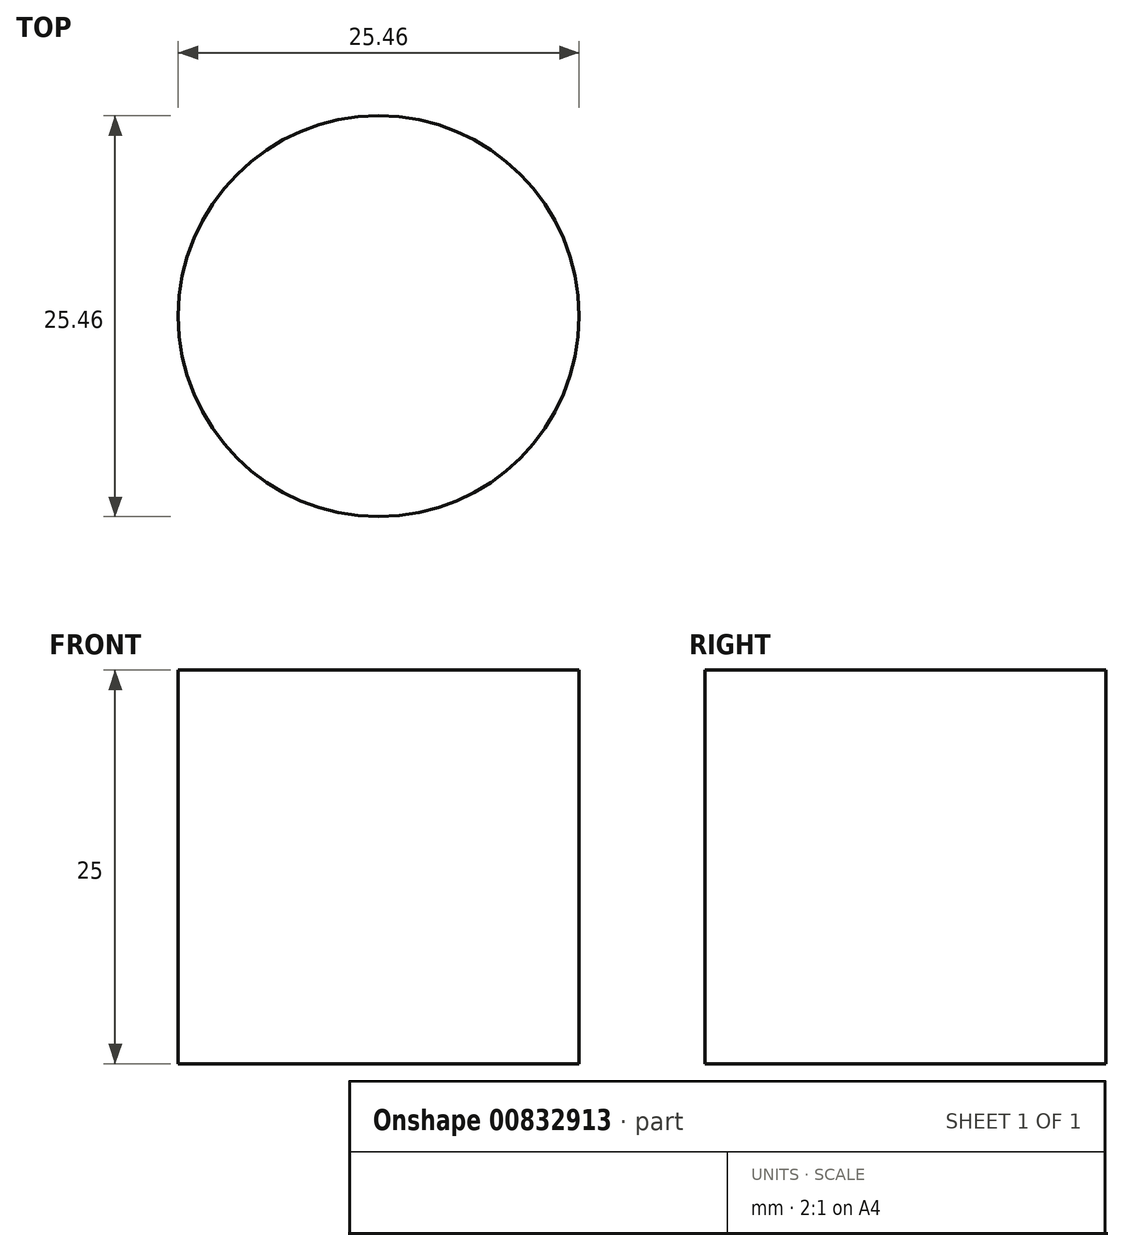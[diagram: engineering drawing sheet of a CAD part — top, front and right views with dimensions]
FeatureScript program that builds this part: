
annotation { "Feature Type Name" : "Feature", "Feature Type Description" : "" }
export const myFeature = defineFeature(function(context is Context, id is Id, definition is map)
    precondition{}
    {
        {
            var Q0;
            Q0=qCreatedBy(makeId("Top.planeOp"),FACE);
            var sketch = newSketch(context, id + "F0", { "sketchPlane" : qUnion([Q0])});
            skCircle(sketch, "E0", {"center": v(0, 0) * mm, "radius": 12.73 * mm});
            skSolve(sketch);
        }
        {
            var Q0;
            Q0=makeQuery(id+"F0.imprint","IMPRINT",FACE,{"disambiguationData":[TD([[makeQuery(id+"F0.imprint","IMPRINT",EDGE,{"derivedFrom":sQuery(id+"F0.wireOp",EDGE,"E0")}),1.0]])]});
            extrude(context, id + "F1", {"entities" : qUnion([Q0]), "depth" : 25 * mm, "offsetDistance" : 25 * mm});
        }
    });
